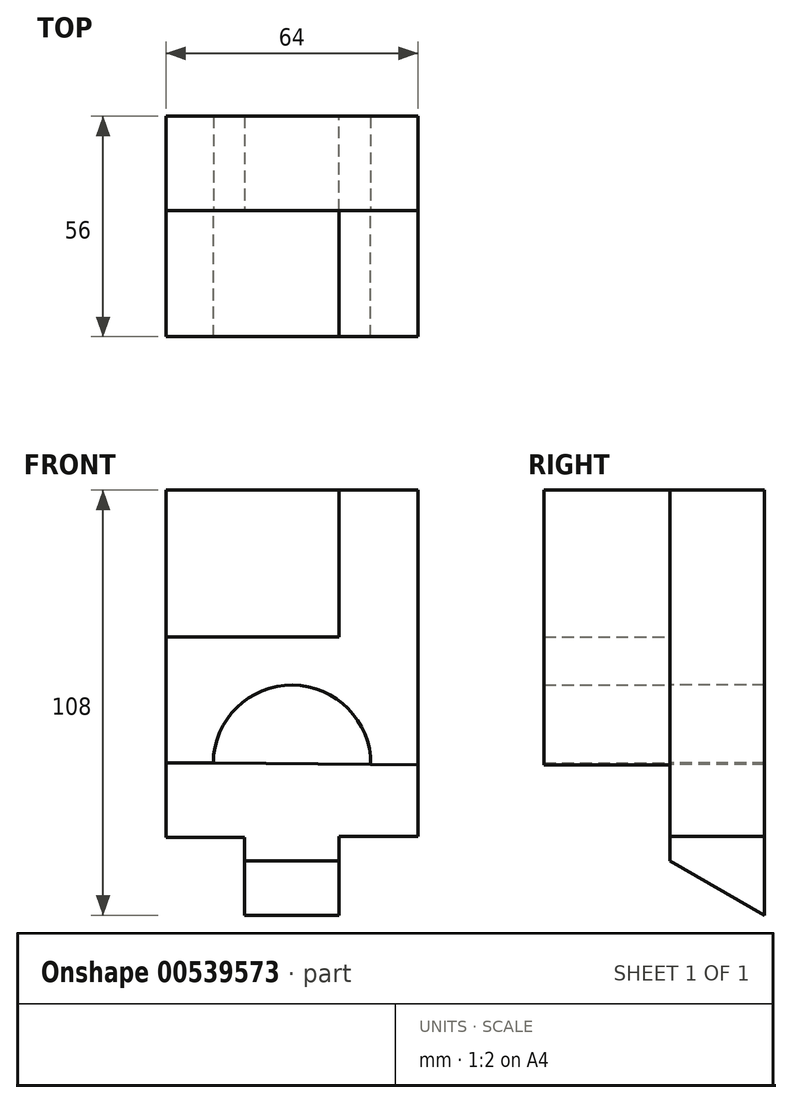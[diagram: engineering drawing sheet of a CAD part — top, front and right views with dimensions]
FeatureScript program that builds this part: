
annotation { "Feature Type Name" : "Feature", "Feature Type Description" : "" }
export const myFeature = defineFeature(function(context is Context, id is Id, definition is map)
    precondition{}
    {
        {
            var Q0;
            Q0=qCreatedBy(makeId("Front.planeOp"),FACE);
            var sketch = newSketch(context, id + "F0", { "sketchPlane" : qUnion([Q0])});
            skLineSegment(sketch, "E0.bottom", {"start": v(35.01, -54) * mm, "end": v(-28.99, -54) * mm});
            skLineSegment(sketch, "E0.top", {"start": v(35.01, 54) * mm, "end": v(-28.99, 54) * mm});
            skLineSegment(sketch, "E0.left", {"start": v(35.01, -54) * mm, "end": v(35.01, 54) * mm});
            skLineSegment(sketch, "E0.right", {"start": v(-28.99, -54) * mm, "end": v(-28.99, 54) * mm});
            skPoint(sketch, "E0.middle", {"position": v(3.01, 0) * mm});
            skSolve(sketch);
        }
        {
            var Q0;
            Q0=makeQuery(id+"F0.imprint","IMPRINT",FACE,{"disambiguationData":[TD([[makeQuery(id+"F0.imprint","IMPRINT",EDGE,{"derivedFrom":sQuery(id+"F0.wireOp",EDGE,"E0.bottom")}),-1.0]])]});
            extrude(context, id + "F1", {"entities" : qUnion([Q0]), "depth" : 24 * mm, "offsetDistance" : 25 * mm});
        }
        {
            var Q0;
            Q0=makeQuery(id+"F1.opExtrude","CAP_FACE",FACE,{"disambiguationData":[OSD([sQuery(id+"F0.wireOp",EDGE,"E0.bottom"),sQuery(id+"F0.wireOp",EDGE,"E0.top"),sQuery(id+"F0.wireOp",EDGE,"E0.left"),sQuery(id+"F0.wireOp",EDGE,"E0.right")])],"isStart":false});
            var sketch = newSketch(context, id + "F2", { "sketchPlane" : qUnion([Q0])});
            skLineSegment(sketch, "E1", {"start": v(15.01, 54) * mm, "end": v(15.01, 16.76) * mm});
            skLineSegment(sketch, "E2", {"start": v(15.01, 16.76) * mm, "end": v(-28.99, 16.76) * mm});
            skLineSegment(sketch, "E3", {"start": v(-28.99, 16.76) * mm, "end": v(-28.99, -15.24) * mm});
            skLineSegment(sketch, "E4", {"start": v(-28.99, -15.24) * mm, "end": v(35.01, -15.79) * mm});
            skArc(sketch, "E5", {"start": v(23.01, -15.69) * mm, "mid": v(3.18, 4.48) * mm, "end": v(-16.99, -15.34) * mm});
            skSolve(sketch);
        }
        {
            var Q0;
            {var subQ1=sQuery(id+"F2.wireOp",EDGE,"E1");Q0=makeQuery(id+"F2.imprint","IMPRINT",FACE,{"disambiguationData":[TD([[makeQuery(id+"F2.imprint","IMPRINT",EDGE,{"derivedFrom":subQ1}),1.0]])]});}
            extrude(context, id + "F3", {"entities" : qUnion([Q0]), "depth" : 32 * mm, "offsetDistance" : 25 * mm});
        }
        {
            var Q0;
            Q0 = qSketchRegion(id + "F2", true);
            extrude(context, id + "F4", {"entities" : qUnion([Q0]), "oppositeDirection" : true, "depth" : 24 * mm, "offsetDistance" : 25 * mm});
        }
        {
            var Q0;
            {var subQ4=sQuery(id+"F2.wireOp",EDGE,"E1");Q0=makeQuery(id+"F2.imprint","IMPRINT",FACE,{"disambiguationData":[TD([[makeQuery(id+"F2.imprint","IMPRINT",EDGE,{"derivedFrom":subQ4}),-1.0]])]});}
            var sketch = newSketch(context, id + "F5", { "sketchPlane" : qUnion([Q0])});
            skLineSegment(sketch, "E6", {"start": v(-29.03, -34.2) * mm, "end": v(-9.03, -34.2) * mm});
            skLineSegment(sketch, "E7", {"start": v(-29.03, -34.2) * mm, "end": v(-29.03, -54.2) * mm});
            skLineSegment(sketch, "E8", {"start": v(-29.03, -54.2) * mm, "end": v(34.97, -54.2) * mm});
            skLineSegment(sketch, "E9", {"start": v(-9.03, -34.2) * mm, "end": v(-9.03, -54.2) * mm});
            skLineSegment(sketch, "E10.MirrorCS", {"start": v(14.97, -34.2) * mm, "end": v(14.97, -54.2) * mm});
            skLineSegment(sketch, "E11.MirrorCS", {"start": v(34.97, -34.2) * mm, "end": v(14.97, -34.2) * mm});
            skLineSegment(sketch, "E12.MirrorCS", {"start": v(34.97, -34.2) * mm, "end": v(34.97, -54.2) * mm});
            skSolve(sketch);
        }
        {
            var Q0;
            Q0 = qSketchRegion(id + "F5", true);
            extrude(context, id + "F6", {"entities" : qUnion([Q0]), "operationType" : NewBodyOperationType.REMOVE, "oppositeDirection" : true, "depth" : 25 * mm, "offsetDistance" : 25 * mm});
        }
        {
            var Q0;
            Q0=makeQuery(id+"F1.opExtrude","SWEPT_FACE",FACE,{"disambiguationData":[OSD([sQuery(id+"F0.wireOp",EDGE,"E0.bottom")])]});
            var sketch = newSketch(context, id + "F7", { "sketchPlane" : qUnion([Q0])});
            skLineSegment(sketch, "E13.bottom", {"start": v(14.97, 24) * mm, "end": v(35.01, 24) * mm});
            skLineSegment(sketch, "E13.top", {"start": v(14.97, 0) * mm, "end": v(35.01, 0) * mm});
            skLineSegment(sketch, "E13.left", {"start": v(14.97, 24) * mm, "end": v(14.97, 0) * mm});
            skLineSegment(sketch, "E13.right", {"start": v(35.01, 24) * mm, "end": v(35.01, 0) * mm});
            skSolve(sketch);
        }
        {
            var Q0;
            Q0 = qSketchRegion(id + "F7", true);
            extrude(context, id + "F8", {"entities" : qUnion([Q0]), "operationType" : NewBodyOperationType.REMOVE, "oppositeDirection" : true, "depth" : 20 * mm, "offsetDistance" : 25 * mm});
        }
        {
            var Q0;
            Q0=makeQuery(id+"F6.boolean.opBoolean","COPY",FACE,{"derivedFrom":makeQuery(id+"F6.opExtrude","SWEPT_FACE",FACE,{"disambiguationData":[OSD([sQuery(id+"F5.wireOp",EDGE,"E9")])]})});
            var sketch = newSketch(context, id + "F9", { "sketchPlane" : qUnion([Q0])});
            skLineSegment(sketch, "E14", {"start": v(24, -34.2) * mm, "end": v(24, -40.2) * mm});
            skLineSegment(sketch, "E15", {"start": v(24, -40.2) * mm, "end": v(0, -54) * mm});
            skSolve(sketch);
        }
        {
            var Q0;
            {var subQ0=sQuery(id+"F9.wireOp",EDGE,"E15");Q0=makeQuery(id+"F9.imprint","IMPRINT",FACE,{"disambiguationData":[TD([[makeQuery(id+"F9.imprint","IMPRINT",EDGE,{"derivedFrom":subQ0}),1.0]])]});}
            extrude(context, id + "F10", {"entities" : qUnion([Q0]), "operationType" : NewBodyOperationType.REMOVE, "oppositeDirection" : true, "depth" : 25 * mm, "offsetDistance" : 25 * mm});
        }
    });
